# Revit family: Panel-Solar_Baxi_Paneles-Solares-Planos_SOL200
name_source: partatom
category: Equipos mecánicos
units: mm (PartAtom-declared; Revit-internal decimal feet)

## family parameters
Anfitrión = Cara
Compartido = No
Corte con vacíos al cargar = No
Cota de conector redondo = Diámetro de uso
Punto de cálculo de habitación = No
Tipo de pieza = Normal

## types (2) — shared parameters
Absorbancia % = 95.00%
Absorbedor = De aluminio, con tratamiento
altamente selectivo
Aislamiento posterior = Fibra de vidrio con velo negro de 40 mm
Autor = Bimetica Parametric Design Services S.L.
Bimetica = http://www.bimetica.com
Carcasa = De aluminio en color gris RAL7016
Carcasa_Mat = Aluminio Lacado Gris RAL 7016
Circuito hidráulico = Serpentín
Colectores por fila = Hasta 10
Descripción = Colectores solares altamente selectivos de 2 o 2'5 m2 de área total. Modelo SOL 200 / SOL 250 para instalación en vertical y SOL 200 H  / SOL 250 H para instalación en horizontal. Permite la instalación de hasta 10 colectores por fila conexionados en paralelo.
Diámetro Exterior - Serpentín Entrada = 22 mm
Diámetro Interior - Serpentín Entrada = 20 mm
Diámetro Interior - Serpentín Salida = 20 mm
Diámetro exterior - Serpentín Salida = 22 mm
Emitancia % = 5.00%
Fabricante = Baxi Calefacción, S.L.U.
FechaEmisionElementoBIM = 04/05/2016
FechaVencimientoElementoBIM = 01/01/2017
Flujo Retorno hidrónico = 0.0 L/s
Flujo Suministro hidrónico = 0.0 L/s
Grosor (mm) = 87 mm  [stored 0.285433 ft]
MasterformatCodigo = 23 56 13
MasterformatTitulo = Heating Solar Collectors
NumeroSerie = Paneles Solares Planos Sol 200
OmniclassCodigo = 23.19.25.11.19.15
OmniclassTitulo = Solar Panels
PeriodoGarantia = 10 años
Presión máx. trabajo = 10.0 baria
ReferenciaContacto = Departamento Técnico
Serpentín_Mat = Cobre
TelefonoContacto = 902 89 89 89
UNSPSCCodigo = 60104701
UNSPSCTitulo = Solar collecting devices
URL = www.baxi.es
URLProducto = https://www.baxi.es
Uniclass2.0Codigo = 60-60-81
Uniclass2.0Titulo = Solar collectors
Vidrio solar = Texturizado 3,2 mm.
Vidrio solar_Mat = Vidrio Solar Texturizado
zero-valued in all types: Elevación por defecto, Espesor absorbedor (mm)

## per-type parameters (varying)
| type | Alto (mm) | Capacidad | Contraseña certificación | Ecuación característica | Instalación | Largo (mm) | Peso vacío | Referencia | Sol 200 | Sol 200H | Temp. estancamiento |
| Sol 200 | 1753 mm  [stored 5.75131 ft] | 1.9 L | GPS-8417 | Ƞ = 0,817 - 3,716 T* - 0,018 GT*² | Vertical | 1147 mm | 34.00 kg | 720364001 | Sí | No | 213 °C |
| Sol 200 H | 1147 mm | 2.2 L | GPS-8420 | Ƞ= 0,809 - 3,989 T* - 0,017 GT*² | Horizontal | 1753 mm  [stored 5.75131 ft] | 35.00 kg | 720364301 | No | Sí | 211 °C |

note: column(s) folded — value = type name in every type: Modelo

note: [stored X ft] marks values corroborated as IEEE doubles in the binary element streams (Revit-internal decimal feet)
